# Revit family: EAE_ORI_36W_40
name_source: partatom
category: Lighting Fixtures
revit_build: Autodesk Revit 2017 (Build: 20160225_1515(x64)
units: mm (PartAtom-declared; Revit-internal decimal feet)

## family parameters
Cut with Voids When Loaded = Yes
Host = Face
Light Source = Yes
OmniClass Number = 23.80.70.11.14.11
OmniClass Title = Downlights
Part Type = Normal
Room Calculation Point = No
Round Connector Dimension = Use Diameter
Shared = No

## types (1)
- 37W 4000K
    Apparent Load = 39 VA
    Ballast Number of Poles = 1
    Body Material = EAE Body Material
    Body Material 2 = EAE White Aluminum
    Color Filter = 0
    Color Options = 3000K
    Default Elevation = 1200 mm
    DiameteR 2 = 115 mm  [stored 0.377297 ft]
    Diameter = 125 mm  [stored 0.410105 ft]
    Diffuser Material = Glass(White)
    Dimming Lamp Color Temperature Shift = <None>
    Emit Shape Visible in Rendering = No
    Emit from Circle Diameter = 115 mm  [stored 0.377297 ft]
    Height = 111 mm
    IP Grade = IP20
    Lamp = COB LED
    Load Classification = Lighting
    Manufacturer = EAE
    Model = ORI
    Modeled By = EAE
    Operation Temperature Range = -20°C/+35°C
    Order Code = 3088715
    Photometric Web File = generic
    Power = 35 VA
    Power Factor = 0.9
    Product Code = ORI 037A 40CM00 50 LLL 80 YV
    Tilt Angle = 90.00°
    URL = https://eaelighting.com
    Voltage = 220 V
    Weight = 0.60 kg

note: [stored X ft] marks values corroborated as IEEE doubles in the binary element streams (Revit-internal decimal feet)

## geometry (parser evidence)
native form markers: Blend x2, Sweep x6
no freeform markers — native parametric forms only
